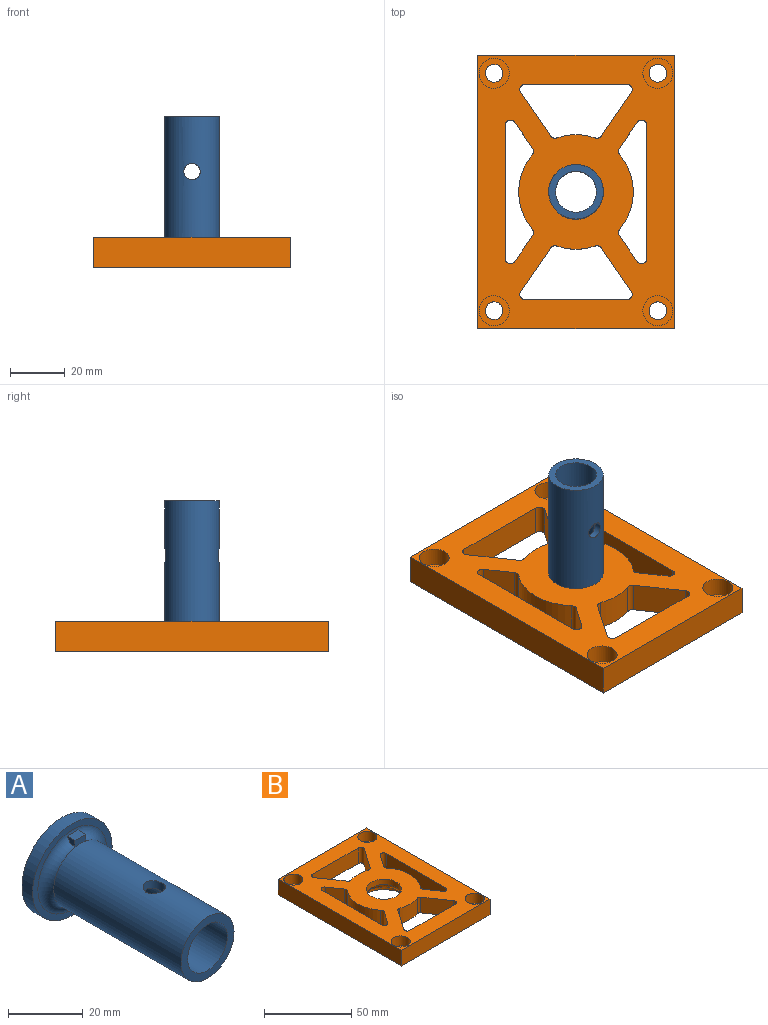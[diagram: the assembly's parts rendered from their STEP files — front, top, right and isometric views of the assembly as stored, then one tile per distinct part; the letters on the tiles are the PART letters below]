
ASSEMBLY  parts=2 mates=1
PART A: 13 faces, bbox 32.8x55x32.8 mm
  f0: cylinder r=7.5mm len=55mm, axis (0,-1,0), area 2534.1mm2, adj f4,f9,f11,f12
  f1: cylinder r=10mm len=48mm, axis (0,1,0), area 2958.8mm2, adj f8,f9,f10,f11,f12
  f2: plane 30x30mm, normal (0,-1,0), area 175.9mm2, adj f3,f10
  f3: cylinder r=15mm len=30mm, axis (0,-1,0), area 377mm2, adj f2,f4
  f4: plane 30x30mm, normal (0,1,0), area 530.1mm2, adj f0,f3
  f5: plane 2.89x2.21mm, normal (1,0,0), area 4.7mm2, adj f6,f8,f10
  f6: plane 4x2.88mm, normal (0,0,1), area 11.4mm2, adj f5,f7,f8,f10
  f7: plane 2.89x2.21mm, normal (-1,0,0), area 4.7mm2, adj f6,f8,f10
  f8: plane 4x2.2mm, normal (0,-1,0), area 8.3mm2, adj f1,f5,f6,f7
  f9: plane 20x20mm, normal (0,-1,0), area 137.4mm2, adj f0,f1
  f10: torus R=13mm, axis (0,-1,0), area 313.3mm2, adj f1,f2,f5,f6,f7
  f11: cylinder r=3mm len=6mm, axis (0,0,-1), area 48.6mm2, adj f0,f1
  f12: cylinder r=3mm len=6mm, axis (0,0,-1), area 48.7mm2, adj f0,f1
PART B: 58 faces, bbox 72.1x100.1x11.1 mm
  f0: plane 11x11mm, normal (0,0,1), area 61.9mm2, adj f28,f34
  f1: plane 11x11mm, normal (0,0,1), area 61.9mm2, adj f19,f33
  f2: plane 11x11mm, normal (0,0,1), area 61.9mm2, adj f20,f32
  f3: plane 11x11mm, normal (0,0,1), area 61.9mm2, adj f21,f31
  f4: plane 72x11mm, normal (0,1,0), area 792mm2, adj f5,f22,f29,f35
  f5: plane 100x11mm, normal (-1,0,0), area 1100mm2, adj f4,f6,f29,f35
  f6: plane 72x11mm, normal (0,-1,0), area 792mm2, adj f5,f22,f29,f35
  f7: plane 48.46x11mm, normal (1,0,0), area 533.1mm2, adj f29,f35,f54,f57
  f8: plane 11x9.36mm, normal (-0.82,-0.57,0), area 125.1mm2, adj f29,f35,f54,f55
  f9: cylinder r=21mm len=27.16mm, axis (0,0,1), area 324.8mm2, adj f29,f35,f55,f56
  f10: plane 15.82x11mm, normal (0.82,-0.57,0), area 211.3mm2, adj f29,f35,f50,f53
  f11: cylinder r=21mm len=14mm, axis (0,0,1), area 157mm2, adj f29,f35,f50,f51
  f12: plane 15.82x11mm, normal (-0.82,-0.57,0), area 211.3mm2, adj f29,f35,f51,f52
  f13: cylinder r=21mm len=14mm, axis (0,0,1), area 157mm2, adj f29,f35,f46,f49
  f14: plane 15.82x11mm, normal (0.82,0.57,0), area 211.3mm2, adj f29,f35,f46,f47
  f15: plane 37.15x11mm, normal (0,-1,0), area 408.6mm2, adj f29,f35,f47,f48
  f16: plane 48.46x11mm, normal (-1,0,0), area 533.1mm2, adj f29,f35,f42,f45
  f17: plane 11x9.36mm, normal (0.82,0.57,0), area 125.1mm2, adj f29,f35,f42,f43
  f18: cylinder r=21mm len=27.16mm, axis (0,0,1), area 324.8mm2, adj f29,f35,f43,f44
  f19: cylinder r=3.25mm len=6.5mm, axis (0,0,1), area 81.7mm2, adj f1,f29
  f20: cylinder r=3.25mm len=6.5mm, axis (0,0,1), area 81.7mm2, adj f2,f29
  f21: cylinder r=3.25mm len=6.5mm, axis (0,0,1), area 81.7mm2, adj f3,f29
  f22: plane 100x11mm, normal (1,0,0), area 1100mm2, adj f4,f6,f29,f35
  f23: plane 11x9.36mm, normal (-0.82,0.57,0), area 125.1mm2, adj f29,f35,f56,f57
  f24: plane 37.15x11mm, normal (0,1,0), area 408.6mm2, adj f29,f35,f52,f53
  f25: plane 15.82x11mm, normal (-0.82,0.57,0), area 211.3mm2, adj f29,f35,f48,f49
  f26: cylinder r=15.05mm len=30.1mm, axis (0,0,1), area 378.2mm2, adj f29,f36
  f27: plane 11x9.36mm, normal (0.82,-0.57,0), area 125.1mm2, adj f29,f35,f44,f45
  f28: cylinder r=3.25mm len=6.5mm, axis (0,0,1), area 81.7mm2, adj f0,f29
  f29: plane 100x72mm, normal (0,0,-1), area 4440.7mm2, adj f4,f5,f6,f7,f8,f9,f10,f11
  f30: cylinder r=10.05mm len=20.1mm, axis (0,0,-1), area 246.3mm2, adj f35,f37,f41
  f31: cylinder r=5.5mm len=11mm, axis (0,0,-1), area 241.9mm2, adj f3,f35
  f32: cylinder r=5.5mm len=11mm, axis (0,0,-1), area 241.9mm2, adj f2,f35
  f33: cylinder r=5.5mm len=11mm, axis (0,0,-1), area 241.9mm2, adj f1,f35
  f34: cylinder r=5.5mm len=11mm, axis (0,0,-1), area 241.9mm2, adj f0,f35
  f35: plane 100x72mm, normal (0,0,1), area 4587.6mm2, adj f4,f5,f6,f7,f8,f9,f10,f11
  f36: plane 30.1x30.1mm, normal (0,0,-1), area 168.3mm2, adj f26,f37
  f37: torus R=13.15mm, axis (0,0,1), area 326.2mm2, adj f30,f36,f38,f39,f40
  f38: plane 3.14x2.46mm, normal (-1,0,0), area 5.1mm2, adj f37,f39,f41
  f39: plane 4.1x2.99mm, normal (0,-1,0), area 12.1mm2, adj f37,f38,f40,f41
  f40: plane 3.14x2.46mm, normal (1,0,0), area 5.1mm2, adj f37,f39,f41
  f41: plane 4.1x2.31mm, normal (0,0,-1), area 8.9mm2, adj f30,f38,f39,f40
  f42: cylinder r=2mm len=11mm, axis (0,0,-1), area 55.8mm2, adj f16,f17,f29,f35
  f43: cylinder r=2mm len=11mm, axis (0,0,1), area 28.8mm2, adj f17,f18,f29,f35
  f44: cylinder r=2mm len=11mm, axis (0,0,1), area 28.8mm2, adj f18,f27,f29,f35
  f45: cylinder r=2mm len=11mm, axis (0,0,1), area 55.8mm2, adj f16,f27,f29,f35
  f46: cylinder r=2mm len=11mm, axis (0,0,1), area 28.8mm2, adj f13,f14,f29,f35
  f47: cylinder r=2mm len=11mm, axis (0,0,-1), area 47.8mm2, adj f14,f15,f29,f35
  f48: cylinder r=2mm len=11mm, axis (0,0,-1), area 47.8mm2, adj f15,f25,f29,f35
  f49: cylinder r=2mm len=11mm, axis (0,0,1), area 28.8mm2, adj f13,f25,f29,f35
  f50: cylinder r=2mm len=11mm, axis (0,0,1), area 28.8mm2, adj f10,f11,f29,f35
  f51: cylinder r=2mm len=11mm, axis (0,0,1), area 28.8mm2, adj f11,f12,f29,f35
  f52: cylinder r=2mm len=11mm, axis (0,0,-1), area 47.8mm2, adj f12,f24,f29,f35
  f53: cylinder r=2mm len=11mm, axis (0,0,-1), area 47.8mm2, adj f10,f24,f29,f35
  f54: cylinder r=2mm len=11mm, axis (0,0,1), area 55.8mm2, adj f7,f8,f29,f35
  f55: cylinder r=2mm len=11mm, axis (0,0,1), area 28.8mm2, adj f8,f9,f29,f35
  f56: cylinder r=2mm len=11mm, axis (0,0,1), area 28.8mm2, adj f9,f23,f29,f35
  f57: cylinder r=2mm len=11mm, axis (0,0,-1), area 55.8mm2, adj f7,f23,f29,f35
PLACE A rot(axis=(-1,0,0),90deg) t=(0.99,-1.89,-5.76)mm
PLACE B t=(0.99,-1.89,-5.76)mm fixed
MATE fastened B.f26 <-> A.f3  axis (0,0,1) through (0.99,-1.89,-7.76)mm
